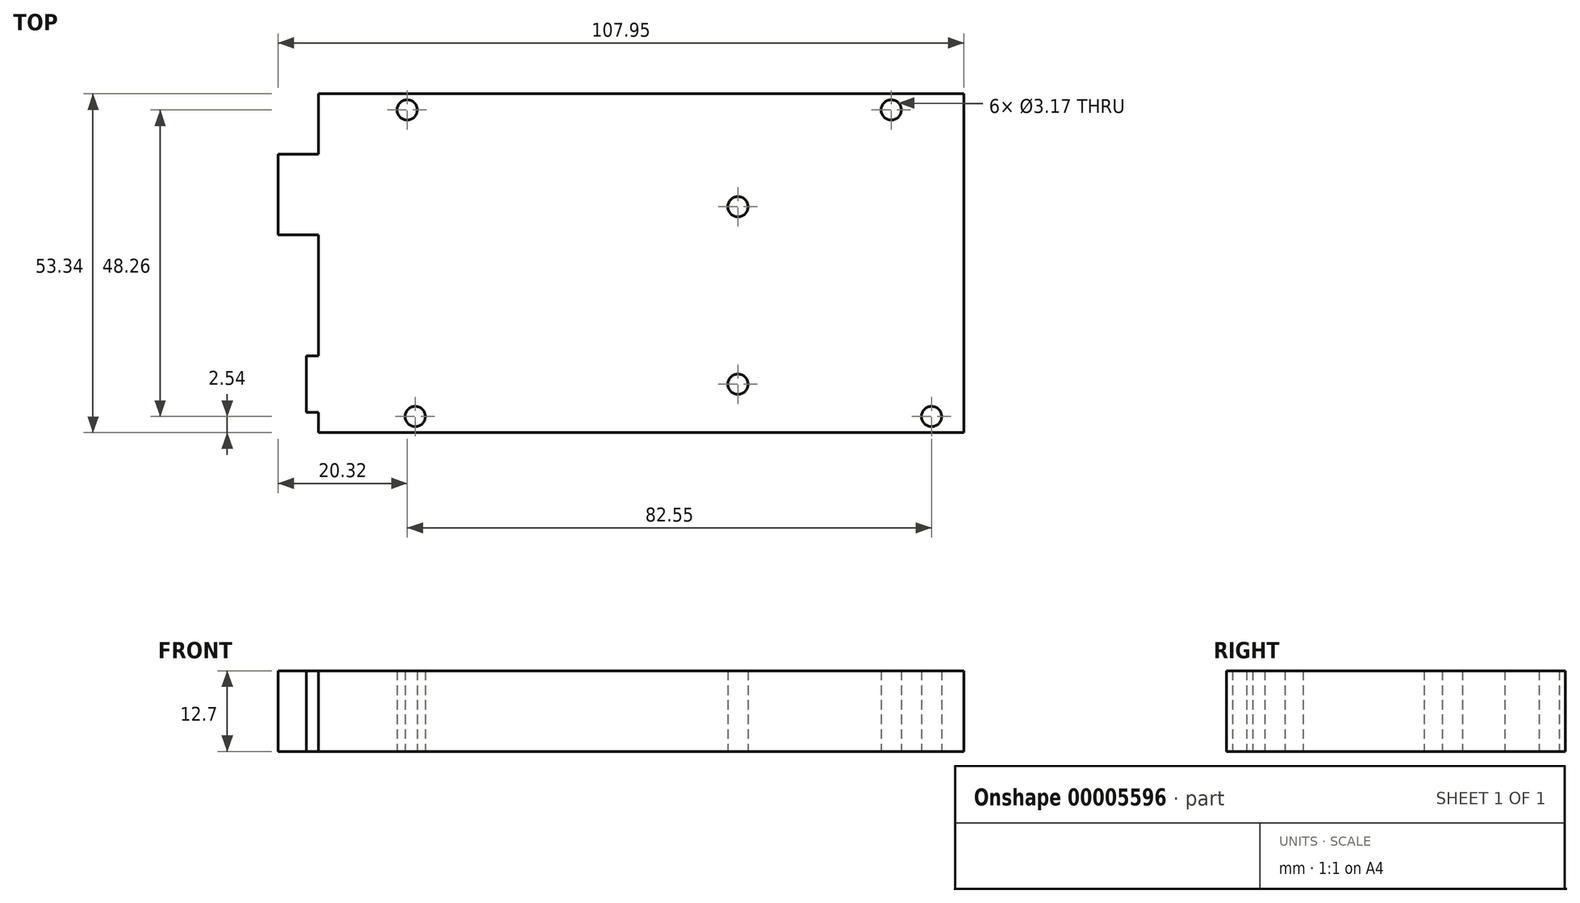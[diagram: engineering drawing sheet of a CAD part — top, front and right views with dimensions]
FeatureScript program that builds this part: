
annotation { "Feature Type Name" : "Feature", "Feature Type Description" : "" }
export const myFeature = defineFeature(function(context is Context, id is Id, definition is map)
    precondition{}
    {
        {
            var Q0;
            Q0=qCreatedBy(makeId("Top.planeOp"),FACE);
            var sketch = newSketch(context, id + "F0", { "sketchPlane" : qUnion([Q0])});
            skLineSegment(sketch, "E0.bottom", {"start": v(-50.8, 26.67) * mm, "end": v(50.8, 26.67) * mm, "construction": true});
            skLineSegment(sketch, "E0.top", {"start": v(-50.8, -26.67) * mm, "end": v(50.8, -26.67) * mm, "construction": true});
            skLineSegment(sketch, "E0.left", {"start": v(-50.8, 26.67) * mm, "end": v(-50.8, -26.67) * mm, "construction": true});
            skLineSegment(sketch, "E0.right", {"start": v(50.8, 26.67) * mm, "end": v(50.8, -26.67) * mm, "construction": true});
            skCircle(sketch, "E1", {"center": v(-35.56, -24.13) * mm, "radius": 1.59 * mm});
            skCircle(sketch, "E2", {"center": v(45.72, -24.13) * mm, "radius": 1.59 * mm});
            skCircle(sketch, "E3", {"center": v(39.37, 24.13) * mm, "radius": 1.59 * mm});
            skCircle(sketch, "E4", {"center": v(-36.83, 24.13) * mm, "radius": 1.59 * mm});
            skCircle(sketch, "E5", {"center": v(15.24, 8.89) * mm, "radius": 1.59 * mm});
            skCircle(sketch, "E6", {"center": v(15.24, -19.05) * mm, "radius": 1.59 * mm});
            skLineSegment(sketch, "E7.bottom", {"start": v(-57.15, 17.15) * mm, "end": v(-39.37, 17.15) * mm});
            skLineSegment(sketch, "E7.top", {"start": v(-57.15, 4.45) * mm, "end": v(-39.37, 4.45) * mm});
            skLineSegment(sketch, "E7.left", {"start": v(-57.15, 17.15) * mm, "end": v(-57.15, 4.45) * mm});
            skLineSegment(sketch, "E7.right", {"start": v(-39.37, 17.15) * mm, "end": v(-39.37, 4.45) * mm});
            skLineSegment(sketch, "E8.bottom", {"start": v(-52.7, -14.6) * mm, "end": v(-39.37, -14.6) * mm});
            skLineSegment(sketch, "E8.top", {"start": v(-52.7, -23.5) * mm, "end": v(-39.37, -23.5) * mm});
            skLineSegment(sketch, "E8.left", {"start": v(-52.7, -14.6) * mm, "end": v(-52.7, -23.5) * mm});
            skLineSegment(sketch, "E8.right", {"start": v(-39.37, -14.6) * mm, "end": v(-39.37, -23.5) * mm});
            skLineSegment(sketch, "E9.bottom", {"start": v(-50.8, 26.67) * mm, "end": v(50.8, 26.67) * mm});
            skLineSegment(sketch, "E9.top", {"start": v(-50.8, -26.67) * mm, "end": v(50.8, -26.67) * mm});
            skLineSegment(sketch, "E9.left", {"start": v(-50.8, 26.67) * mm, "end": v(-50.8, -26.67) * mm});
            skLineSegment(sketch, "E9.right", {"start": v(50.8, 26.67) * mm, "end": v(50.8, -26.67) * mm});
            skSolve(sketch);
        }
        {
            var Q0;
            {var subQ5=sQuery(id+"F0.wireOp",EDGE,"E7.left");Q0=makeQuery(id+"F0.imprint","IMPRINT",FACE,{"disambiguationData":[TD([[makeQuery(id+"F0.imprint","IMPRINT",EDGE,{"derivedFrom":subQ5}),1.0]])]});}
            var Q1;
            {var subQ5=sQuery(id+"F0.wireOp",EDGE,"E8.left");Q1=makeQuery(id+"F0.imprint","IMPRINT",FACE,{"disambiguationData":[TD([[makeQuery(id+"F0.imprint","IMPRINT",EDGE,{"derivedFrom":subQ5}),1.0]])]});}
            var Q2;
            {var subQ5=sQuery(id+"F0.wireOp",EDGE,"E7.right");Q2=makeQuery(id+"F0.imprint","IMPRINT",FACE,{"disambiguationData":[TD([[makeQuery(id+"F0.imprint","IMPRINT",EDGE,{"derivedFrom":subQ5}),-1.0]])]});}
            var Q3;
            {var subQ5=sQuery(id+"F0.wireOp",EDGE,"E8.right");Q3=makeQuery(id+"F0.imprint","IMPRINT",FACE,{"disambiguationData":[TD([[makeQuery(id+"F0.imprint","IMPRINT",EDGE,{"derivedFrom":subQ5}),-1.0]])]});}
            var Q4;
            Q4=makeQuery(id+"F0.imprint","IMPRINT",FACE,{"disambiguationData":[TD([[makeQuery(id+"F0.imprint","IMPRINT",EDGE,{"derivedFrom":sQuery(id+"F0.wireOp",EDGE,"E1")}),-1.0]])]});
            extrude(context, id + "F1", {"entities" : qUnion([Q0, Q1, Q2, Q3, Q4]), "depth" : 12.7 * mm, "symmetric" : true});
        }
    });
